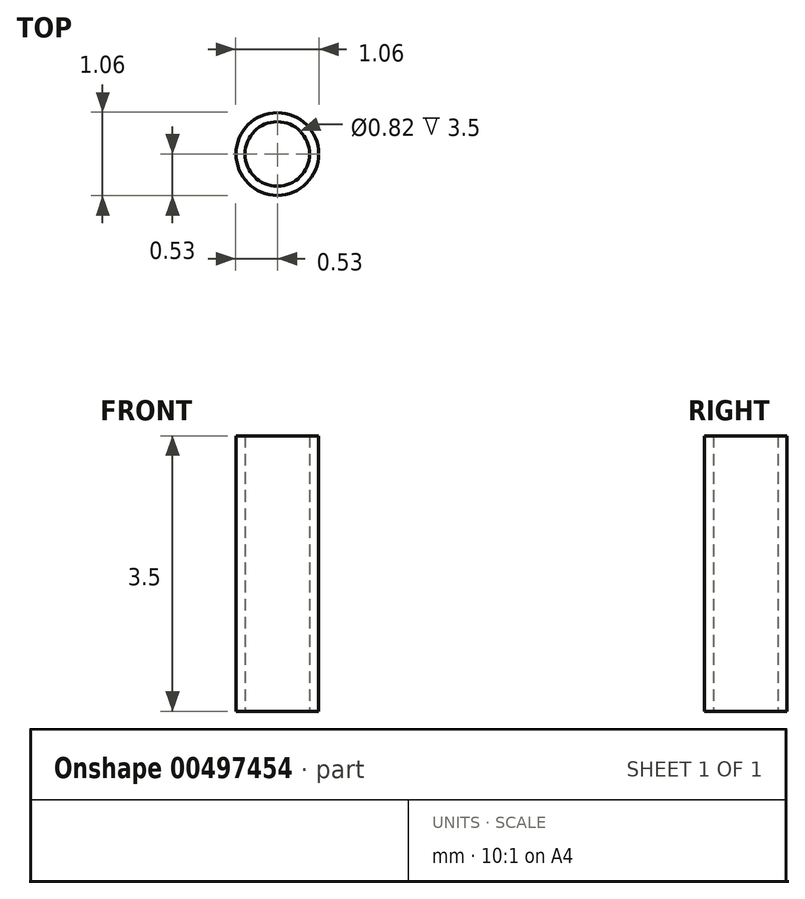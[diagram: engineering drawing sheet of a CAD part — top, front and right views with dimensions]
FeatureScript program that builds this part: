
annotation { "Feature Type Name" : "Feature", "Feature Type Description" : "" }
export const myFeature = defineFeature(function(context is Context, id is Id, definition is map)
    precondition{}
    {
        {
            var Q0;
            Q0=qCreatedBy(makeId("Top.planeOp"),FACE);
            var sketch = newSketch(context, id + "F0", { "sketchPlane" : qUnion([Q0])});
            skCircle(sketch, "E0", {"center": v(0, 0) * mm, "radius": 0.41 * mm});
            skCircle(sketch, "E1", {"center": v(0, 0) * mm, "radius": 0.53 * mm});
            skSolve(sketch);
        }
        {
            var Q0;
            Q0=makeQuery(id+"F0.imprint","IMPRINT",FACE,{"disambiguationData":[TD([[makeQuery(id+"F0.imprint","IMPRINT",EDGE,{"derivedFrom":sQuery(id+"F0.wireOp",EDGE,"E0")}),-1.0]])]});
            extrude(context, id + "F1", {"entities" : qUnion([Q0]), "depth" : 3.5 * mm});
        }
    });
